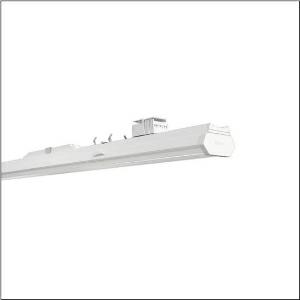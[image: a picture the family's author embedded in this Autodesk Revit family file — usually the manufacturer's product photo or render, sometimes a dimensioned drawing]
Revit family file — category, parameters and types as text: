
# Revit family: licross_11_protected_mo_51td11cn49xg
name_source: partatom
category: Lighting Fixtures
units: mm (PartAtom-declared; Revit-internal decimal feet)

## family parameters
Cut with Voids When Loaded = No
Host = Face
Light Source = No
Part Type = Normal
Room Calculation Point = No
Round Connector Dimension = Use Diameter
Shared = No

## types (1)
- --- (1 x LED, 9030 lm, 49.4 W, 4000K)
    Apparent Load = 49 VA
    CIE Flux Codes = 83 94 98 100 100
    Color Rendering = 80
    Color Temperature = 4000K
    Default Elevation = 1800 mm
    Description = Licross 11 Protected MO, luminaire insert, of sheet steel, galvanised, coil coated, white, length: 1.500mm, width: 90mm, height: 101mm, LED rated luminous flux: 9.030lm, light colour: 840, SDCM (Standard Deviation of Colour Matching)MacAdam ≤ 2 SDCM (initial), control gear: ON/OFF Multilumen, CLOi, with plug, 3-pole, with phase selection, mains connection: 220..240V, AC, 50/60Hz, start of lifetime: 49W, end of service life: 55W, internal wiring halogen-free, primary light control with lens, of plastic, primary optical cover: cover, of PMMA, light emission: direct distribution, primary light characteristic: symmetric, protection rating (complete): IP54, insulation class (complete): insulation class I (protective earthing), certification: CE, ENEC, VDE, UKCA, protection symbol: D if used in an environment with non-conductive dust loads with corresponding accessories, impact resistance: IK06, permissible ambient temperature for indoor applications: -35..+40°C, corresponds to IFS (International Featured Standards) requirements for safety and quality in the food industry, reducing of maximum allowable ambient temperature of 5°C with ceiling mounting, LABS conformity tested according to VDMA 24364:2018-05, The light source and the operating device comply with the requirements of the Ecodesign Regulation (EU) 2019/2020 and are replaceable in accordance with this regulation, packaging unit: 1 piece
    Height = 92 mm
    Lamp = 1 x LED
    Lamp Light Flux = 9030 lm
    Lamp Power = 49.4 W
    Lamp count = 1
    Length = 1500 mm
    Luminous efficacy = 183 lm/W
    Manufacturer = Siteco
    ModVariant = No
    Model = 51TD11CN49XG
    Mounting Place = Ceiling
    Mounting Type = Pendant
    Number of Poles = 1
    OnlyDefault = Yes
    Power Factor = 1
    Product Name = Licross 11 Protected MO
    Product group = luminaire insert | ceiling pendant
    ProductGroupID = 901
    Protection Class = Protection class I
    Protection Degree = IP 54
    RLX_Detail_Level = 1
    RLX_Emergency_Light_Flux = 0 lm
    RLX_Emergency_Type = 0
    RLX_Emergency_Type_DB = No
    RlxData = <blob elided: 22089 chars, md5=34f0896f>
    Socket = socket
    Standby Power = 0 W
    System Light Flux = 9030 lm
    System Power = 49 W
    Type Comments = factory setting: luminous flux: 100 % | (A | C | E) | 113 mA
    Type Image = l_1256145.jpg
    URL = http://relux.com
    VarID = @adj_091101
    Voltage = 0 V
    Weight = 0.00 kg
    Width = 88 mm

## geometry (parser evidence)
native form markers: Blend x4, Sweep x9
no freeform markers — native parametric forms only
